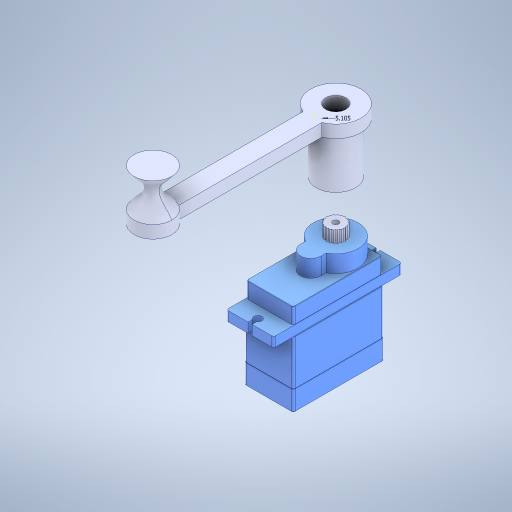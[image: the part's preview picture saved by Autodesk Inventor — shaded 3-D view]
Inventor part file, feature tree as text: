
AUTODESK INVENTOR PART (.ipt)
format: ipt  version: 2024 (Build 280153000, 153)  size: 647,168 bytes
history: native  units: in
note: dims shown in document units (in); Inventor stores cm internally (conversion verified against a paired STEP export)
features: sketch x8, plane x5, extrude x3, other x2, loft x1
ambient origin geometry x8: Origin, YZ Plane, XZ Plane, XY Plane, X Axis, Y Axis, Z Axis, Center Point
bodies: Solid1 (feature_tree)
feature tree (19):
  plane  "Work Plane1"
  extrude  "Main Shaft (thingy with the pattern on it)"  Depth=0.3937in
  plane  "Work Plane2"
  sketch  "Sketch9"  dims[d0=0.3937in d19=0.3911in]
  extrude  "Extrusion8"  Depth=0.5in
  sketch  "Sketch11"  dims[d63=0.5in d64=0.125in d65=0.0in]
  plane  "Work Plane4"
  sketch  "Sketch12"  dims[d68=1.418in d69=0.188in]
  sketch  "Sketch13"  dims[d70=0.375in]
  plane  "Work Plane5"
  sketch  "Sketch14"  dims[d71=0.375in]
  plane  "Work Plane6"
  loft  "Loft1"
  extrude  "Extrusion9"  Depth=0.188in
  other  "STILL NEEDS CONSTRAINTS"
  sketch  "Sketch10"  dims[d34=0.5in d35=0.0in d45=0.0787in]
  sketch  "Sketch15"  dims[d72=0.375in]
  sketch  "Sketch16"  dims[d73=0.375in d74=0.1875in d75=0.125in d76=-0.094in d77=0.0in d78=90.0deg d79=0.0in d80=90.0deg d81=0.0in d82=90.0deg d83=0.0in d84=90.0deg d85=0.201in d86=0.375in d87=0.0in d222=0.0109in d223=0.201in d54=0.0197in d55=0.0344in d56=0.0197in d57=0.0344in d60=0.0in d61=0.0in d62=0.0in]
  other  "Yükseklik-Ekstrüzyon7"
